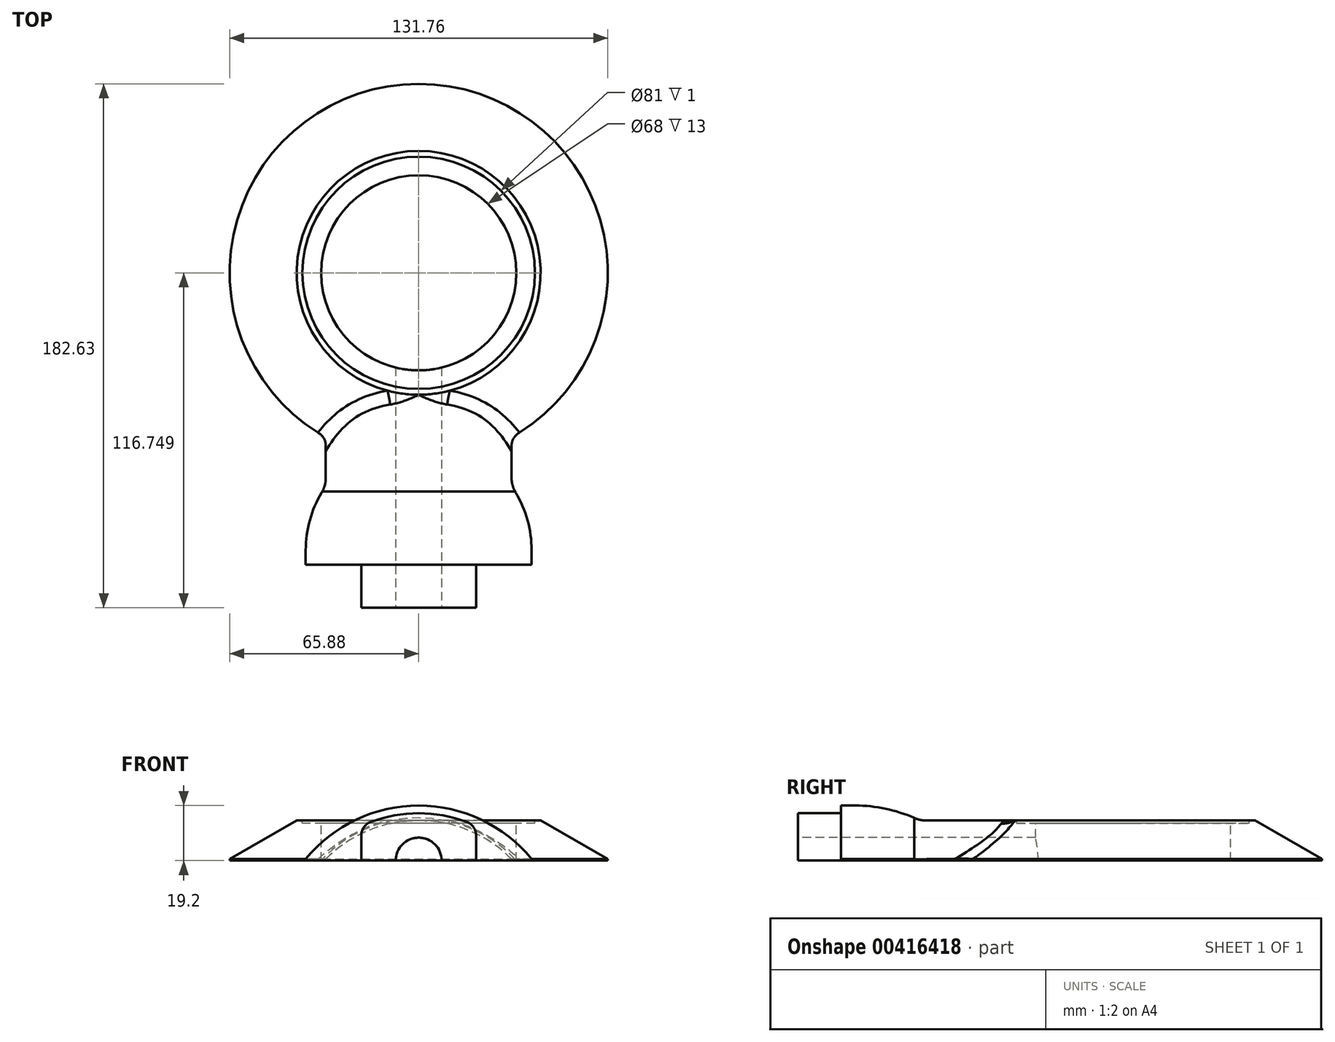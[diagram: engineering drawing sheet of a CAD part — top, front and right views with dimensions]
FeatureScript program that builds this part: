
annotation { "Feature Type Name" : "Feature", "Feature Type Description" : "" }
export const myFeature = defineFeature(function(context is Context, id is Id, definition is map)
    precondition{}
    {
        {
            var Q0;
            Q0=qCreatedBy(makeId("Front.planeOp"),FACE);
            var sketch = newSketch(context, id + "F0", { "sketchPlane" : qUnion([Q0])});
            skLineSegment(sketch, "E0", {"start": v(-39.5, 0) * mm, "end": v(39.5, 0) * mm});
            skPoint(sketch, "E1", {"position": v(0, 19) * mm});
            skLineSegment(sketch, "E2", {"start": v(39.5, 0) * mm, "end": v(39.5, 0) * mm});
            skLineSegment(sketch, "E3.MirrorCS", {"start": v(-39.5, 0) * mm, "end": v(-39.5, 0) * mm});
            skArc(sketch, "E4", {"start": v(39.5, 0) * mm, "mid": v(0, 19) * mm, "end": v(-39.5, 0) * mm});
            skSolve(sketch);
        }
        {
            var Q0;
            Q0=qCreatedBy(makeId("Front.planeOp"),FACE);
            var sketch = newSketch(context, id + "F1", { "sketchPlane" : qUnion([Q0])});
            skLineSegment(sketch, "E5.0", {"start": v(-39.35, 0) * mm, "end": v(0, 0) * mm});
            skArc(sketch, "E6.0", {"start": v(0, 19.2) * mm, "mid": v(-21.79, 14.29) * mm, "end": v(-39.35, 0.5) * mm});
            skLineSegment(sketch, "E7", {"start": v(-39.35, 0.5) * mm, "end": v(-39.35, 0) * mm});
            skArc(sketch, "E8.MirrorCS", {"start": v(0, 19.2) * mm, "mid": v(21.79, 14.29) * mm, "end": v(39.35, 0.5) * mm});
            skLineSegment(sketch, "E9.MirrorCS", {"start": v(39.35, 0.5) * mm, "end": v(39.35, 0) * mm});
            skLineSegment(sketch, "E10.MirrorCS", {"start": v(39.35, 0) * mm, "end": v(0, 0) * mm});
            skSolve(sketch);
        }
        {
            var Q0;
            Q0=qCreatedBy(makeId("Front.planeOp"),FACE);
            var sketch = newSketch(context, id + "F2", { "sketchPlane" : qUnion([Q0])});
            skArc(sketch, "E11.0", {"start": v(20, 12.14) * mm, "mid": v(0, 16.5) * mm, "end": v(-20, 12.14) * mm});
            skLineSegment(sketch, "E12", {"start": v(-20, 0) * mm, "end": v(20, 0) * mm});
            skLineSegment(sketch, "E13", {"start": v(20, 0) * mm, "end": v(20, 12.14) * mm});
            skLineSegment(sketch, "E14.MirrorCS", {"start": v(-20, 0) * mm, "end": v(-20, 12.14) * mm});
            skPoint(sketch, "E15.orphan", {"position": v(-36.25, 0) * mm});
            skSolve(sketch);
        }
        {
            var Q0;
            Q0=qCreatedBy(makeId("Right.planeOp"),FACE);
            var sketch = newSketch(context, id + "F3", { "sketchPlane" : qUnion([Q0])});
            skLineSegment(sketch, "E16", {"start": v(163.5, 0) * mm, "end": v(96.75, 0) * mm, "construction": true});
            skLineSegment(sketch, "E17", {"start": v(30.87, 0.5) * mm, "end": v(54.25, 14) * mm});
            skLineSegment(sketch, "E18", {"start": v(54.25, 14) * mm, "end": v(96.75, 14) * mm});
            skLineSegment(sketch, "E19", {"start": v(139.25, 14) * mm, "end": v(163.5, 0) * mm, "construction": true});
            skLineSegment(sketch, "E20", {"start": v(96.75, 0) * mm, "end": v(96.75, 41.66) * mm, "construction": true});
            skLineSegment(sketch, "E21", {"start": v(96.75, 14) * mm, "end": v(96.75, 0) * mm});
            skLineSegment(sketch, "E22", {"start": v(96.75, 14) * mm, "end": v(139.25, 14) * mm, "construction": true});
            skLineSegment(sketch, "E23", {"start": v(96.75, 0) * mm, "end": v(30.87, 0) * mm});
            skLineSegment(sketch, "E24", {"start": v(30.87, 0.5) * mm, "end": v(30.87, 0) * mm});
            skPoint(sketch, "E25.orphan", {"position": v(30, 0) * mm});
            skSolve(sketch);
        }
        {
            var Q0;
            Q0=qSketchRegion(id+"F3",true);
            var Q1;
            Q1=sQuery(id+"F3.wireOp",EDGE,"E20");
            revolve(context, id + "F4", {"entities" : qUnion([Q0]), "axis" : qUnion([Q1]), "revolveType" : RevolveType.FULL});
        }
        {
            var Q0;
            Q0=qSketchRegion(id+"F1",true);
            extrude(context, id + "F5", {"entities" : qUnion([Q0]), "operationType" : NewBodyOperationType.ADD, "depth" : 5 * mm});
        }
        {
            var Q0;
            Q0=makeQuery(id+"F4.opRevolve","SWEPT_FACE",FACE,{"disambiguationData":[OSD([sQuery(id+"F3.wireOp",EDGE,"E18")])]});
            var sketch = newSketch(context, id + "F6", { "sketchPlane" : qUnion([Q0])});
            skCircle(sketch, "E26", {"center": v(0, 96.75) * mm, "radius": 40.5 * mm});
            skSolve(sketch);
        }
        {
            var Q0;
            Q0=qSketchRegion(id+"F6",true);
            extrude(context, id + "F7", {"entities" : qUnion([Q0]), "operationType" : NewBodyOperationType.REMOVE, "oppositeDirection" : true, "depth" : 1 * mm});
        }
        {
            var Q0;
            Q0=qSketchRegion(id+"F2",true);
            extrude(context, id + "F8", {"entities" : qUnion([Q0]), "operationType" : NewBodyOperationType.ADD, "depth" : 20 * mm});
        }
        {
            var Q0;
            Q0=makeQuery(id+"F7.boolean.opBoolean","COPY",FACE,{"derivedFrom":makeQuery(id+"F7.opExtrude","CAP_FACE",FACE,{"disambiguationData":[OSD([sQuery(id+"F6.wireOp",EDGE,"E26")])],"isStart":false})});
            var sketch = newSketch(context, id + "F9", { "sketchPlane" : qUnion([Q0])});
            skCircle(sketch, "E27", {"center": v(0, 96.75) * mm, "radius": 34 * mm});
            skSolve(sketch);
        }
        {
            var Q0;
            Q0=qSketchRegion(id+"F9",true);
            extrude(context, id + "F10", {"entities" : qUnion([Q0]), "operationType" : NewBodyOperationType.REMOVE, "endBound" : BoundingType.THROUGH_ALL, "oppositeDirection" : true, "depth" : 25 * mm});
        }
        {
            var Q0;
            Q0=makeQuery(id+"F8.opExtrude","SWEPT_EDGE",EDGE,{"disambiguationData":[OSD([sQuery(id+"F2.wireOp",EDGE,"E11.0"),sQuery(id+"F2.wireOp",EDGE,"E13")])]});
            var Q1;
            Q1=makeQuery(id+"F8.opExtrude","SWEPT_EDGE",EDGE,{"disambiguationData":[OSD([sQuery(id+"F2.wireOp",EDGE,"E11.0"),sQuery(id+"F2.wireOp",EDGE,"E14.MirrorCS")])]});
            fillet(context, id + "F11", {"entities" : qUnion([Q0, Q1]), "radius" : 5 * mm, "tangentPropagation" : true, "allowEdgeOverflow" : false});
        }
        {
            var Q0;
            Q0=makeQuery(id+"F5.opExtrude","CAP_FACE",FACE,{"disambiguationData":[OSD([sQuery(id+"F1.wireOp",EDGE,"E5.0"),sQuery(id+"F1.wireOp",EDGE,"E6.0"),sQuery(id+"F1.wireOp",EDGE,"E7"),sQuery(id+"F1.wireOp",EDGE,"E8.MirrorCS"),sQuery(id+"F1.wireOp",EDGE,"E9.MirrorCS"),sQuery(id+"F1.wireOp",EDGE,"E10.MirrorCS")])],"isStart":false});
            var sketch = newSketch(context, id + "F12", { "sketchPlane" : qUnion([Q0])});
            skArc(sketch, "E28.0", {"start": v(32.37, 0.5) * mm, "mid": v(0, 14) * mm, "end": v(-32.37, 0.5) * mm});
            skLineSegment(sketch, "E29", {"start": v(-32.37, 0) * mm, "end": v(32.37, 0) * mm});
            skLineSegment(sketch, "E30", {"start": v(32.37, 0) * mm, "end": v(32.37, 0.5) * mm});
            skLineSegment(sketch, "E31.MirrorCS", {"start": v(-32.37, 0) * mm, "end": v(-32.37, 0.5) * mm});
            skSolve(sketch);
        }
        {
            var Q0;
            Q0=qSketchRegion(id+"F12",true);
            var Q1;
            Q1=makeQuery(id+"F4.opRevolve","SWEPT_FACE",FACE,{"disambiguationData":[OSD([sQuery(id+"F3.wireOp",EDGE,"E17")])]});
            extrude(context, id + "F13", {"entities" : qUnion([Q0]), "operationType" : NewBodyOperationType.ADD, "oppositeDirection" : true, "endBoundEntityFace" : qUnion([Q1]), "depth" : 60 * mm});
        }
        {
            var Q0;
            Q0=makeQuery(id+"F13.boolean.opBoolean","INTERSECT",EDGE,{"disambiguationData":[OD(1.0)],"derivedFrom":[makeQuery(id+"F4.opRevolve","SWEPT_FACE",FACE,{"disambiguationData":[OSD([sQuery(id+"F3.wireOp",EDGE,"E17")])]}),makeQuery(id+"F13.opExtrude","SWEPT_FACE",FACE,{"disambiguationData":[OSD([sQuery(id+"F12.wireOp",EDGE,"E28.0")])]})]});
            fillet(context, id + "F14", {"entities" : qUnion([Q0]), "radius" : 10 * mm, "tangentPropagation" : true, "allowEdgeOverflow" : false});
        }
        {
            var Q0;
            Q0=qCreatedBy(makeId("Front.planeOp"),FACE);
            var sketch = newSketch(context, id + "F15", { "sketchPlane" : qUnion([Q0])});
            skArc(sketch, "E32.0", {"start": v(0, 19.2) * mm, "mid": v(-21.79, 14.29) * mm, "end": v(-39.35, 0.5) * mm});
            skLineSegment(sketch, "E33.0", {"start": v(-39.35, 0.5) * mm, "end": v(-39.35, 0) * mm});
            skLineSegment(sketch, "E34", {"start": v(-39.35, 0) * mm, "end": v(0, 0) * mm});
            skLineSegment(sketch, "E35", {"start": v(0, 0) * mm, "end": v(0, 19.2) * mm});
            skSolve(sketch);
        }
        {
            var Q0;
            Q0 = qSketchRegion(id + "F15", true);
            var Q1;
            Q1=sQuery(id+"F15.wireOp",EDGE,"E35");
            revolve(context, id + "F16", {"operationType" : NewBodyOperationType.ADD, "entities" : qUnion([Q0]), "axis" : qUnion([Q1]), "revolveType" : RevolveType.ONE_DIRECTION, "oppositeDirection" : true, "angle" : 180 * degree});
        }
        {
            var Q0;
            Q0=makeQuery(id+"F16.boolean.opBoolean","INTERSECT",EDGE,{"derivedFrom":[makeQuery(id+"F13.opExtrude","SWEPT_FACE",FACE,{"disambiguationData":[OSD([sQuery(id+"F12.wireOp",EDGE,"E28.0")])]}),makeQuery(id+"F16.opRevolve","SWEPT_FACE",FACE,{"disambiguationData":[OSD([sQuery(id+"F15.wireOp",EDGE,"E32.0")])]})]});
            var Q1;
            Q1=makeQuery(id+"F16.boolean.opBoolean","INTERSECT",EDGE,{"derivedFrom":[makeQuery(id+"F13.opExtrude","SWEPT_FACE",FACE,{"disambiguationData":[OSD([sQuery(id+"F12.wireOp",EDGE,"E30")])]}),makeQuery(id+"F16.opRevolve","SWEPT_FACE",FACE,{"disambiguationData":[OSD([sQuery(id+"F15.wireOp",EDGE,"E33.0")])]})]});
            var Q2;
            Q2=makeQuery(id+"F16.boolean.opBoolean","INTERSECT",EDGE,{"derivedFrom":[makeQuery(id+"F13.opExtrude","SWEPT_FACE",FACE,{"disambiguationData":[OSD([sQuery(id+"F12.wireOp",EDGE,"E31.MirrorCS")])]}),makeQuery(id+"F16.opRevolve","SWEPT_FACE",FACE,{"disambiguationData":[OSD([sQuery(id+"F15.wireOp",EDGE,"E33.0")])]})]});
            fillet(context, id + "F17", {"entities" : qUnion([Q0, Q1, Q2]), "radius" : 10 * mm, "tangentPropagation" : true, "allowEdgeOverflow" : false});
        }
        {
            var Q0;
            Q0=qCreatedBy(makeId("Front.planeOp"),FACE);
            var sketch = newSketch(context, id + "F18", { "sketchPlane" : qUnion([Q0])});
            skCircle(sketch, "E36", {"center": v(0, 0) * mm, "radius": 8 * mm});
            skSolve(sketch);
        }
        {
            var Q0;
            Q0=makeQuery(id+"F18.imprint","IMPRINT",FACE,{"disambiguationData":[TD([[makeQuery(id+"F18.imprint","IMPRINT",EDGE,{"derivedFrom":sQuery(id+"F18.wireOp",EDGE,"E36")}),1.0]])]});
            extrude(context, id + "F19", {"entities" : qUnion([Q0]), "operationType" : NewBodyOperationType.REMOVE, "oppositeDirection" : true, "depth" : 70 * mm, "hasSecondDirection" : true, "secondDirectionOppositeDirection" : false, "secondDirectionDepth" : 25 * mm});
        }
        {
            var Q0;
            Q0=makeQuery(id+"F13.boolean.opBoolean","INTERSECT",EDGE,{"derivedFrom":[makeQuery(id+"F4.opRevolve","SWEPT_FACE",FACE,{"disambiguationData":[OSD([sQuery(id+"F3.wireOp",EDGE,"E24")])]}),makeQuery(id+"F13.opExtrude","SWEPT_FACE",FACE,{"disambiguationData":[OSD([sQuery(id+"F12.wireOp",EDGE,"E30")])]})]});
            var Q1;
            Q1=makeQuery(id+"F13.boolean.opBoolean","INTERSECT",EDGE,{"derivedFrom":[makeQuery(id+"F4.opRevolve","SWEPT_FACE",FACE,{"disambiguationData":[OSD([sQuery(id+"F3.wireOp",EDGE,"E24")])]}),makeQuery(id+"F13.opExtrude","SWEPT_FACE",FACE,{"disambiguationData":[OSD([sQuery(id+"F12.wireOp",EDGE,"E31.MirrorCS")])]})]});
            fillet(context, id + "F20", {"entities" : qUnion([Q0, Q1]), "radius" : 5 * mm, "tangentPropagation" : true, "allowEdgeOverflow" : false});
        }
    });
